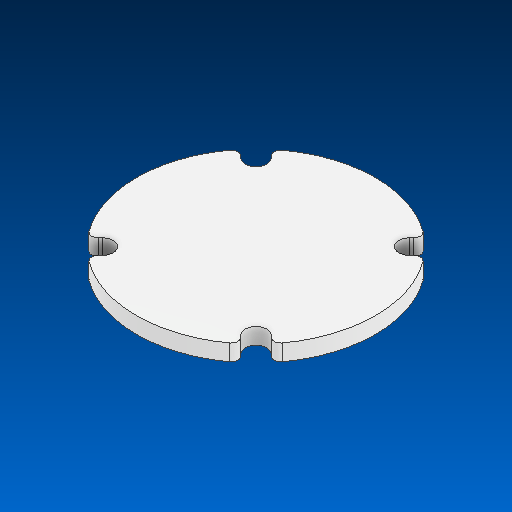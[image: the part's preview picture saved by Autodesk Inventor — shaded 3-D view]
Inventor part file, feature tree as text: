
AUTODESK INVENTOR PART (.ipt)
format: ipt  version: 2022.2 (Build 262287000, 287)  size: 113,152 bytes
history: native  units: in
note: dims shown in document units (in); Inventor stores cm internally (conversion verified against a paired STEP export)
features: fillet x1
ambient origin geometry x8: Origin, YZ Plane, XZ Plane, XY Plane, X Axis, Y Axis, Z Axis, Center Point
bodies: Solid1 (feature_tree)
feature tree (1):
  fillet  "Fillet1"  [1 undecoded]
note: 1 required parameter value undecoded (feature->parameter linkage not recoverable at this tier; creation-order binding heuristic only, values carry confidence <= 0.55)
